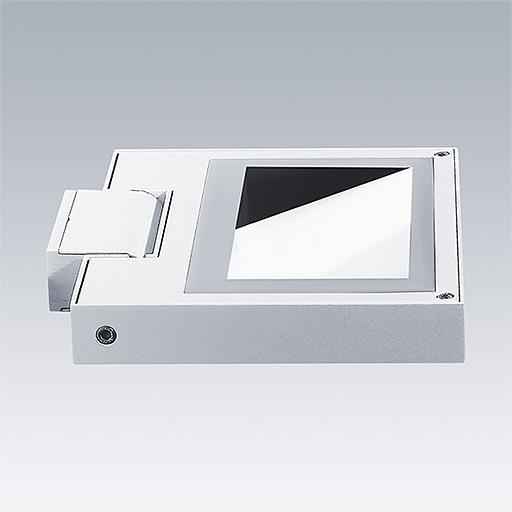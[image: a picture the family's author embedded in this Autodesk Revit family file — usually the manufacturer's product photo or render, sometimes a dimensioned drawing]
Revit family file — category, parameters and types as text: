
# Revit family: Thorn AXYL FLOOD
name_source: partatom
category: Lighting Fixtures
units: mm (PartAtom-declared; Revit-internal decimal feet)

## family parameters
Cut with Voids When Loaded = No
Host = Face
Light Source = No
Maintain Annotation Orientation = No
Part Type = Normal
Room Calculation Point = Yes
Round Connector Dimension = Use Diameter
Shared = No

## types (24) — shared parameters
Apparent Load = 21 VA
Assembly Code = Pr_70_70_48_73
Axyl Flood Arm M = Axyl Flood Rotating Arm : Axyl Flood Arm M
Axyl Flood Arm S = Axyl Flood Rotating Arm : Axyl Flood Arm S
Axyl Flood Type M = Axyl Flood Body : Axyl Flood M
Axyl Flood Type S = Axyl Flood Body : Axyl Flood S
Current = 1 A
Description = Compact asymmetrical LED floodligh
Efficacy = 121 lm/W
Export Type to IFC As = IfcLightFixtureType
Lamp = LED
Manufacturer = Thorn Lighting
Power = 20 VA
Power Factor = 0.97
Type IFC Predefined Type = DIRECTIONSOURCE
URL = https://www.thornlighting.com
zero-valued in all types: Default Elevation

## per-type parameters (varying)
| type | Arm Type | Body Type | D | Housing M | Housing S | Luminaire Height | Luminaire Length | Luminaire Width | Material Housing | Model | Photometric Type | Type Image | Wattage |
| AXYL FLOOD S 56L 927 AS HFX ANT | Axyl Flood Rotating Arm : Axyl Flood Arm S | Axyl Flood Body : Axyl Flood S | -17.5 mm | No | Yes | 34 mm | 220 mm  [stored 0.721785 ft] | 220 mm  [stored 0.721785 ft] | Zumtobel-Aluminium-RAL 7016-Anthracite Grey | 96801558 | Thorn-Light Sources-Axyl-Flood : AXYL FLOOD S 56L 927 AS HFX ANT | TLG_AXYL_F_FLOOD_F_S_56L_ANT.jpg | 18.6 |
| AXYL FLOOD S 56L 927 AS HFX BK | Axyl Flood Rotating Arm : Axyl Flood Arm S | Axyl Flood Body : Axyl Flood S | -17.5 mm | No | Yes | 34 mm | 220 mm  [stored 0.721785 ft] | 220 mm  [stored 0.721785 ft] | Thorn-Aluminium-RAL 9005-Jet Black | 96801556 | Thorn-Light Sources-Axyl-Flood : AXYL FLOOD S 56L 927 AS HFX BK | TLG_AXYL_F_FLOOD_F_S_56L_BK.jpg | 18.6 |
| AXYL FLOOD S 56L 927 AS HFX GY | Axyl Flood Rotating Arm : Axyl Flood Arm S | Axyl Flood Body : Axyl Flood S | -17.5 mm | No | Yes | 34 mm | 220 mm  [stored 0.721785 ft] | 220 mm  [stored 0.721785 ft] | Thorn-Aluminium-RAL 9006-White Aluminium | 96801557 | Thorn-Light Sources-Axyl-Flood : AXYL FLOOD S 56L 927 AS HFX GY | TLG_AXYL_F_FLOOD_F_S_56L_GY.jpg | 18.6 |
| AXYL FLOOD S 56L 927 AS HFX WH | Axyl Flood Rotating Arm : Axyl Flood Arm S | Axyl Flood Body : Axyl Flood S | -17.5 mm | No | Yes | 34 mm | 220 mm  [stored 0.721785 ft] | 220 mm  [stored 0.721785 ft] | Thorn-Aluminium-RAL 9016-Traffic White | 96801555 | Thorn-Light Sources-Axyl-Flood : AXYL FLOOD S 56L 927 AS HFX WH | TLG_AXYL_F_FLOOD_F_S_56L_WH.jpg | 18.6 |
| AXYL FLOOD S 56L 930 AS HFX ANT | Axyl Flood Rotating Arm : Axyl Flood Arm S | Axyl Flood Body : Axyl Flood S | -17.5 mm | No | Yes | 34 mm | 220 mm  [stored 0.721785 ft] | 220 mm  [stored 0.721785 ft] | Zumtobel-Aluminium-RAL 7016-Anthracite Grey | 96801566 | Thorn-Light Sources-Axyl-Flood : AXYL FLOOD S 56L 930 AS HFX ANT | TLG_AXYL_F_FLOOD_F_S_56L_ANT.jpg | 18.6 |
| AXYL FLOOD S 56L 930 AS HFX BK | Axyl Flood Rotating Arm : Axyl Flood Arm S | Axyl Flood Body : Axyl Flood S | -17.5 mm | No | Yes | 34 mm | 220 mm  [stored 0.721785 ft] | 220 mm  [stored 0.721785 ft] | Thorn-Aluminium-RAL 9005-Jet Black | 96801564 | Thorn-Light Sources-Axyl-Flood : AXYL FLOOD S 56L 930 AS HFX BK | TLG_AXYL_F_FLOOD_F_S_56L_BK.jpg | 18.6 |
| AXYL FLOOD S 56L 930 AS HFX GY | Axyl Flood Rotating Arm : Axyl Flood Arm S | Axyl Flood Body : Axyl Flood S | -17.5 mm | No | Yes | 34 mm | 220 mm  [stored 0.721785 ft] | 220 mm  [stored 0.721785 ft] | Thorn-Aluminium-RAL 9006-White Aluminium | 96801565 | Thorn-Light Sources-Axyl-Flood : AXYL FLOOD S 56L 930 AS HFX GY | TLG_AXYL_F_FLOOD_F_S_56L_GY.jpg | 18.6 |
| AXYL FLOOD S 56L 930 AS HFX WH | Axyl Flood Rotating Arm : Axyl Flood Arm S | Axyl Flood Body : Axyl Flood S | -17.5 mm | No | Yes | 34 mm | 220 mm  [stored 0.721785 ft] | 220 mm  [stored 0.721785 ft] | Thorn-Aluminium-RAL 9016-Traffic White | 96801563 | Thorn-Light Sources-Axyl-Flood : AXYL FLOOD S 56L 930 AS HFX WH | TLG_AXYL_F_FLOOD_F_S_56L_WH.jpg | 18.6 |
| AXYL FLOOD S 56L 940 AS HFX ANT | Axyl Flood Rotating Arm : Axyl Flood Arm S | Axyl Flood Body : Axyl Flood S | -17.5 mm | No | Yes | 34 mm | 220 mm  [stored 0.721785 ft] | 220 mm  [stored 0.721785 ft] | Zumtobel-Aluminium-RAL 7016-Anthracite Grey | 96801562 | Thorn-Light Sources-Axyl-Flood : AXYL FLOOD S 56L 940 AS HFX ANT | TLG_AXYL_F_FLOOD_F_S_56L_ANT.jpg | 18.6 |
| AXYL FLOOD S 56L 940 AS HFX BK | Axyl Flood Rotating Arm : Axyl Flood Arm S | Axyl Flood Body : Axyl Flood S | -17.5 mm | No | Yes | 34 mm | 220 mm  [stored 0.721785 ft] | 220 mm  [stored 0.721785 ft] | Thorn-Aluminium-RAL 9005-Jet Black | 96801560 | Thorn-Light Sources-Axyl-Flood : AXYL FLOOD S 56L 940 AS HFX BK | TLG_AXYL_F_FLOOD_F_S_56L_BK.jpg | 18.6 |
| AXYL FLOOD S 56L 940 AS HFX GY | Axyl Flood Rotating Arm : Axyl Flood Arm S | Axyl Flood Body : Axyl Flood S | -17.5 mm | No | Yes | 34 mm | 220 mm  [stored 0.721785 ft] | 220 mm  [stored 0.721785 ft] | Thorn-Aluminium-RAL 9006-White Aluminium | 96801561 | Thorn-Light Sources-Axyl-Flood : AXYL FLOOD S 56L 940 AS HFX GY | TLG_AXYL_F_FLOOD_F_S_56L_GY.jpg | 18.6 |
| AXYL FLOOD S 56L 940 AS HFX WH | Axyl Flood Rotating Arm : Axyl Flood Arm S | Axyl Flood Body : Axyl Flood S | -17.5 mm | No | Yes | 34 mm | 220 mm  [stored 0.721785 ft] | 220 mm  [stored 0.721785 ft] | Thorn-Aluminium-RAL 9016-Traffic White | 96801559 | Thorn-Light Sources-Axyl-Flood : AXYL FLOOD S 56L 940 AS HFX WH | TLG_AXYL_F_FLOOD_F_S_56L_WH.jpg | 18.6 |
| AXYL FLOOD M 126L 927 AS HFX ANT | Axyl Flood Rotating Arm : Axyl Flood Arm M | Axyl Flood Body : Axyl Flood M | -20.5 mm  [stored -0.0672572 ft] | Yes | No | 40 mm  [stored 0.131234 ft] | 295 mm  [stored 0.967848 ft] | 320 mm  [stored 1.04987 ft] | Zumtobel-Aluminium-RAL 7016-Anthracite Grey | 96801570 | Thorn-Light Sources-Axyl-Flood : AXYL FLOOD M 126L 927 AS HFX ANT | TLG_AXYL_F_FLOOD_F_M_126L_ANT.jpg | 39.6 |
| AXYL FLOOD M 126L 927 AS HFX BK | Axyl Flood Rotating Arm : Axyl Flood Arm M | Axyl Flood Body : Axyl Flood M | -20.5 mm  [stored -0.0672572 ft] | Yes | No | 40 mm  [stored 0.131234 ft] | 295 mm  [stored 0.967848 ft] | 320 mm  [stored 1.04987 ft] | Thorn-Aluminium-RAL 9005-Jet Black | 96801568 | Thorn-Light Sources-Axyl-Flood : AXYL FLOOD M 126L 927 AS HFX BK | TLG_AXYL_F_FLOOD_F_M_126L_BK.jpg | 39.6 |
| AXYL FLOOD M 126L 927 AS HFX GY | Axyl Flood Rotating Arm : Axyl Flood Arm M | Axyl Flood Body : Axyl Flood M | -20.5 mm  [stored -0.0672572 ft] | Yes | No | 40 mm  [stored 0.131234 ft] | 295 mm  [stored 0.967848 ft] | 320 mm  [stored 1.04987 ft] | Thorn-Aluminium-RAL 9006-White Aluminium | 96801569 | Thorn-Light Sources-Axyl-Flood : AXYL FLOOD M 126L 927 AS HFX GY | TLG_AXYL_F_FLOOD_F_M_126L_GY.jpg | 39.6 |
| AXYL FLOOD M 126L 927 AS HFX WH | Axyl Flood Rotating Arm : Axyl Flood Arm M | Axyl Flood Body : Axyl Flood M | -20.5 mm  [stored -0.0672572 ft] | Yes | No | 40 mm  [stored 0.131234 ft] | 295 mm  [stored 0.967848 ft] | 320 mm  [stored 1.04987 ft] | Thorn-Aluminium-RAL 9016-Traffic White | 96801567 | Thorn-Light Sources-Axyl-Flood : AXYL FLOOD M 126L 927 AS HFX WH | TLG_AXYL_F_FLOOD_F_M_126L_WH.jpg | 39.6 |
| AXYL FLOOD M 126L 930 AS HFX ANT | Axyl Flood Rotating Arm : Axyl Flood Arm M | Axyl Flood Body : Axyl Flood M | -20.5 mm  [stored -0.0672572 ft] | Yes | No | 40 mm  [stored 0.131234 ft] | 295 mm  [stored 0.967848 ft] | 320 mm  [stored 1.04987 ft] | Zumtobel-Aluminium-RAL 7016-Anthracite Grey | 96801578 | Thorn-Light Sources-Axyl-Flood : AXYL FLOOD M 126L 930 AS HFX ANT | TLG_AXYL_F_FLOOD_F_M_126L_ANT.jpg | 39.6 |
| AXYL FLOOD M 126L 930 AS HFX BK | Axyl Flood Rotating Arm : Axyl Flood Arm M | Axyl Flood Body : Axyl Flood M | -20.5 mm  [stored -0.0672572 ft] | Yes | No | 40 mm  [stored 0.131234 ft] | 295 mm  [stored 0.967848 ft] | 320 mm  [stored 1.04987 ft] | Thorn-Aluminium-RAL 9005-Jet Black | 96801576 | Thorn-Light Sources-Axyl-Flood : AXYL FLOOD M 126L 930 AS HFX BK | TLG_AXYL_F_FLOOD_F_M_126L_BK.jpg | 39.6 |
| AXYL FLOOD M 126L 930 AS HFX GY | Axyl Flood Rotating Arm : Axyl Flood Arm M | Axyl Flood Body : Axyl Flood M | -20.5 mm  [stored -0.0672572 ft] | Yes | No | 40 mm  [stored 0.131234 ft] | 295 mm  [stored 0.967848 ft] | 320 mm  [stored 1.04987 ft] | Thorn-Aluminium-RAL 9006-White Aluminium | 96801577 | Thorn-Light Sources-Axyl-Flood : AXYL FLOOD M 126L 930 AS HFX GY | TLG_AXYL_F_FLOOD_F_M_126L_GY.jpg | 39.6 |
| AXYL FLOOD M 126L 930 AS HFX WH | Axyl Flood Rotating Arm : Axyl Flood Arm M | Axyl Flood Body : Axyl Flood M | -20.5 mm  [stored -0.0672572 ft] | Yes | No | 40 mm  [stored 0.131234 ft] | 295 mm  [stored 0.967848 ft] | 320 mm  [stored 1.04987 ft] | Thorn-Aluminium-RAL 9016-Traffic White | 96801575 | Thorn-Light Sources-Axyl-Flood : AXYL FLOOD M 126L 930 AS HFX WH | TLG_AXYL_F_FLOOD_F_M_126L_WH.jpg | 39.6 |
| AXYL FLOOD M 126L 940 AS HFX ANT | Axyl Flood Rotating Arm : Axyl Flood Arm M | Axyl Flood Body : Axyl Flood M | -20.5 mm  [stored -0.0672572 ft] | Yes | No | 40 mm  [stored 0.131234 ft] | 295 mm  [stored 0.967848 ft] | 320 mm  [stored 1.04987 ft] | Zumtobel-Aluminium-RAL 7016-Anthracite Grey | 96801574 | Thorn-Light Sources-Axyl-Flood : AXYL FLOOD M 126L 940 AS HFX ANT | TLG_AXYL_F_FLOOD_F_M_126L_ANT.jpg | 39.6 |
| AXYL FLOOD M 126L 940 AS HFX BK | Axyl Flood Rotating Arm : Axyl Flood Arm M | Axyl Flood Body : Axyl Flood M | -20.5 mm  [stored -0.0672572 ft] | Yes | No | 40 mm  [stored 0.131234 ft] | 295 mm  [stored 0.967848 ft] | 320 mm  [stored 1.04987 ft] | Thorn-Aluminium-RAL 9005-Jet Black | 96801572 | Thorn-Light Sources-Axyl-Flood : AXYL FLOOD M 126L 940 AS HFX BK | TLG_AXYL_F_FLOOD_F_M_126L_BK.jpg | 39.6 |
| AXYL FLOOD M 126L 940 AS HFX GY | Axyl Flood Rotating Arm : Axyl Flood Arm M | Axyl Flood Body : Axyl Flood M | -20.5 mm  [stored -0.0672572 ft] | Yes | No | 40 mm  [stored 0.131234 ft] | 295 mm  [stored 0.967848 ft] | 320 mm  [stored 1.04987 ft] | Thorn-Aluminium-RAL 9006-White Aluminium | 96801573 | Thorn-Light Sources-Axyl-Flood : AXYL FLOOD M 126L 940 AS HFX GY | TLG_AXYL_F_FLOOD_F_M_126L_GY.jpg | 39.6 |
| AXYL FLOOD M 126L 940 AS HFX WH | Axyl Flood Rotating Arm : Axyl Flood Arm M | Axyl Flood Body : Axyl Flood M | -20.5 mm  [stored -0.0672572 ft] | Yes | No | 40 mm  [stored 0.131234 ft] | 295 mm  [stored 0.967848 ft] | 320 mm  [stored 1.04987 ft] | Thorn-Aluminium-RAL 9016-Traffic White | 96801571 | Thorn-Light Sources-Axyl-Flood : AXYL FLOOD M 126L 940 AS HFX WH | TLG_AXYL_F_FLOOD_F_M_126L_WH.jpg | 39.6 |

note: [stored X ft] marks values corroborated as IEEE doubles in the binary element streams (Revit-internal decimal feet)

## geometry (parser evidence)
native form markers: Sweep x7
no freeform markers — native parametric forms only
